# Revit family: Siebhülse VMU plus
name_source: partatom
category: HLS-Bauteile
units: mm (PartAtom-declared; Revit-internal decimal feet)

## family parameters
Basisbauteil = Fläche
Beim Laden mit Abzugskörper schneiden = Nein
Bemaßung runder Anschluss = Durchmesser verwenden
Beschriftungsausrichtung beibehalten = Nein
Gemeinsam genutzt = Ja
Klassifizierung = Keine
Raumberechnungspunkt = Nein
Teiletyp = Normal

## types (4) — shared parameters
Fabrikat = MKT
Material = Polypropylen
Mengeneinheit = St
Vorgabe-Ansicht = 1219 mm
vpe = 10

## per-type parameters (varying)
| type | Artikelnummer | Bohrerdurchmesser | Brandschutz | D | EAN | Gewicht | Kurztext1 | Kurztext2 | Länge | Länge Dübel | T | d1 | max. zul. Last radial (Fx) bis zu 100 °C | passend für |
| Siebhülse VM-SH 16x 85 | 221828152001 | 16 mm |  | 8 mm  [stored 0.0262467 ft] | 4250928455734 | 0.00 kg | Siebhülse VMU plus VM-SH 16 x 85 mm | passend für Ankerstange VMU plus M8-M10 | 83 mm  [stored 0.27231 ft] | 85 mm  [stored 0.278871 ft] | 85 mm  [stored 0.278871 ft] | 8 mm  [stored 0.0262467 ft] | nein | VMU plus M8-M10 |
| Siebhülse VM-SH 16x130 | 221828153001 | 16 mm | ja | 8 mm  [stored 0.0262467 ft] | 4250928457752 | 0.00 kg | Siebhülse VMU plus VM-SH 16 x 130 mm | passend für Ankerstange VMU plus M8-M10 | 128 mm  [stored 0.419948 ft] | 130 mm  [stored 0.426509 ft] | 130 mm  [stored 0.426509 ft] | 8 mm  [stored 0.0262467 ft] | ja | VMU plus M8-M10 |
| Siebhülse VM-SH 20x 85 | 221828154001 | 20 mm |  | 10 mm  [stored 0.0328084 ft] | 4250928457769 | 0.00 kg | Siebhülse VMU plus VM-SH 20 x 85 mm | passend für Ankerstange VMU plus M12-M16 | 83 mm  [stored 0.27231 ft] | 85 mm  [stored 0.278871 ft] | 85 mm  [stored 0.278871 ft] | 10 mm  [stored 0.0328084 ft] | nein | VMU plus M12-M16 |
| Siebhülse VM-SH 20x130 | 221828154301 | 20 mm | ja | 10 mm  [stored 0.0328084 ft] | 4250928457776 | 0.01 kg | Siebhülse VMU plus VM-SH 20 x 130 mm | passend für Ankerstange VMU plus M12-M16 | 128 mm  [stored 0.419948 ft] | 130 mm  [stored 0.426509 ft] | 130 mm  [stored 0.426509 ft] | 10 mm  [stored 0.0328084 ft] | ja | VMU plus M12-M16 |

note: [stored X ft] marks values corroborated as IEEE doubles in the binary element streams (Revit-internal decimal feet)
